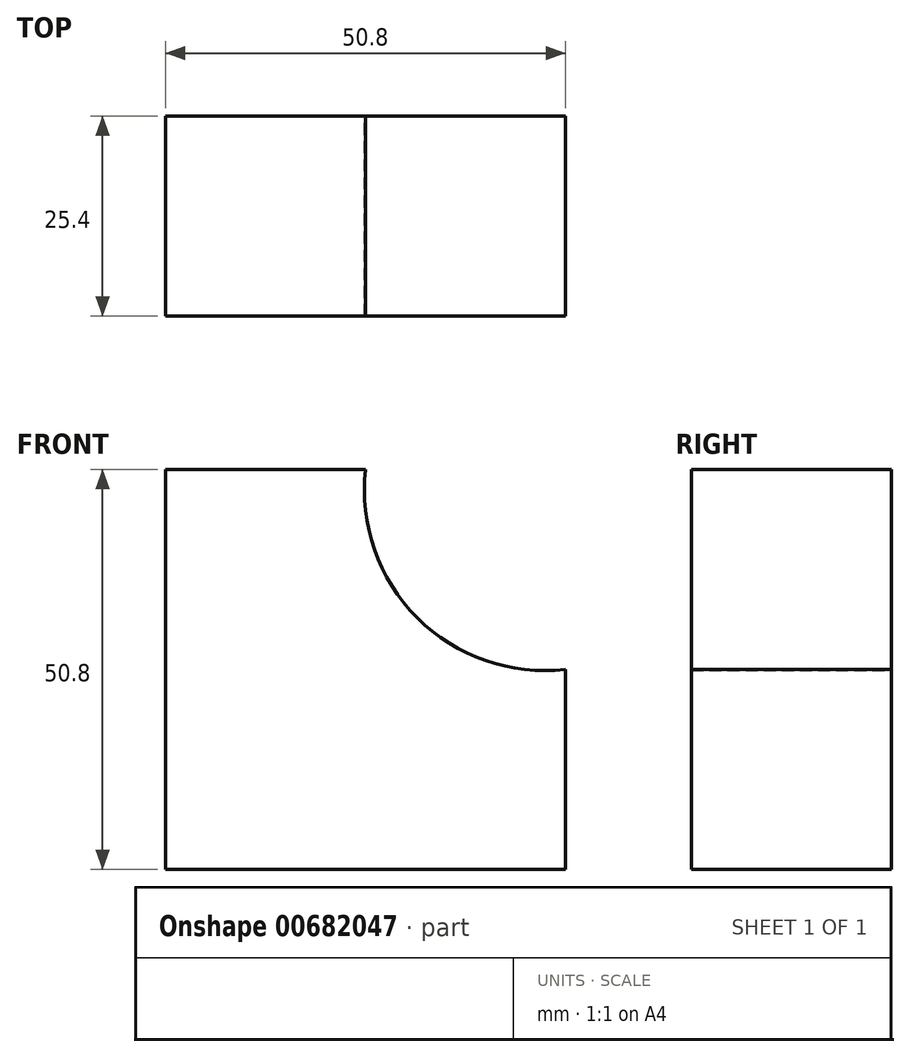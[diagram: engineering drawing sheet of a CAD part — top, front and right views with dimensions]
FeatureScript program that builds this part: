
annotation { "Feature Type Name" : "Feature", "Feature Type Description" : "" }
export const myFeature = defineFeature(function(context is Context, id is Id, definition is map)
    precondition{}
    {
        {
            var Q0;
            Q0=qCreatedBy(makeId("Front.planeOp"),FACE);
            var sketch = newSketch(context, id + "F0", { "sketchPlane" : qUnion([Q0])});
            skLineSegment(sketch, "E0", {"start": v(0, 0) * mm, "end": v(0, 50.8) * mm});
            skLineSegment(sketch, "E1", {"start": v(0, 0) * mm, "end": v(50.8, 0) * mm});
            skLineSegment(sketch, "E2", {"start": v(50.8, 0) * mm, "end": v(50.8, 25.4) * mm});
            skLineSegment(sketch, "E3", {"start": v(0, 50.8) * mm, "end": v(25.4, 50.8) * mm});
            skArc(sketch, "E4", {"start": v(25.4, 50.8) * mm, "mid": v(31.97, 31.97) * mm, "end": v(50.8, 25.4) * mm});
            skSolve(sketch);
        }
        {
            var Q0;
            Q0 = qSketchRegion(id + "F0", true);
            extrude(context, id + "F1", {"entities" : qUnion([Q0]), "depth" : 25.4 * mm, "offsetDistance" : 25.4 * mm});
        }
    });
